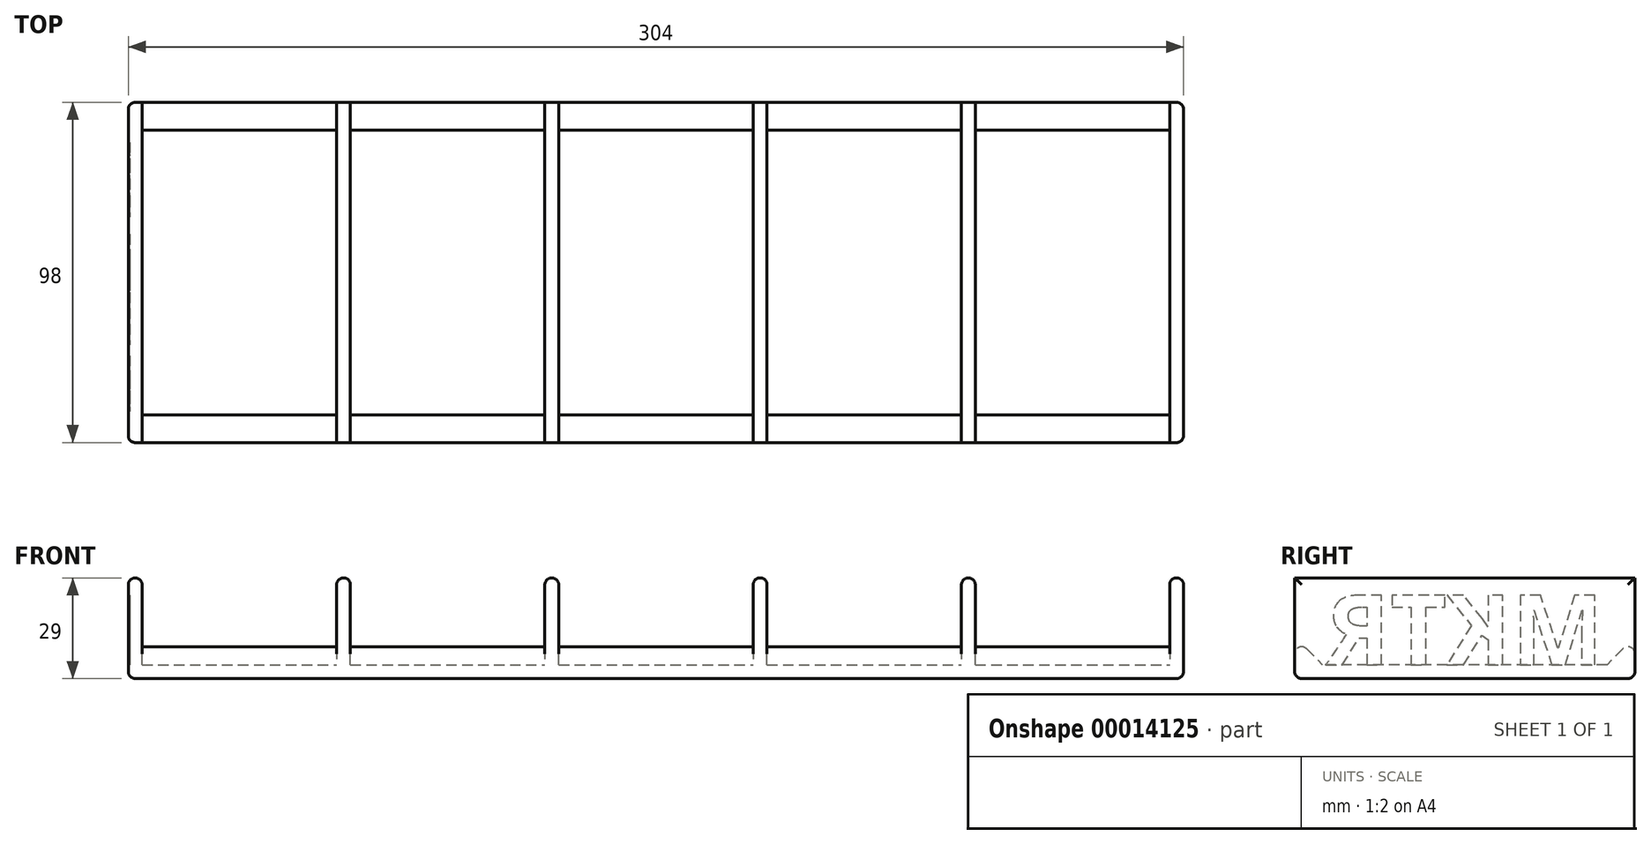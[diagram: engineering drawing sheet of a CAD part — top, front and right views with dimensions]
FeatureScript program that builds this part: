
annotation { "Feature Type Name" : "Feature", "Feature Type Description" : "" }
export const myFeature = defineFeature(function(context is Context, id is Id, definition is map)
    precondition{}
    {
        {
            var Q0;
            Q0=qCreatedBy(makeId("Top.planeOp"),FACE);
            var sketch = newSketch(context, id + "F0", { "sketchPlane" : qUnion([Q0])});
            skLineSegment(sketch, "E0.rect.bottom", {"start": v(-152, 49) * mm, "end": v(152, 49) * mm});
            skLineSegment(sketch, "E0.rect.top", {"start": v(-152, -49) * mm, "end": v(152, -49) * mm});
            skLineSegment(sketch, "E0.rect.left", {"start": v(-152, 49) * mm, "end": v(-152, -49) * mm});
            skLineSegment(sketch, "E0.rect.right", {"start": v(152, 49) * mm, "end": v(152, -49) * mm});
            skPoint(sketch, "E0.rect.middle", {"position": v(0, 0) * mm});
            skSolve(sketch);
        }
        {
            var Q0;
            Q0 = qSketchRegion(id + "F0", true);
            extrude(context, id + "F1", {"entities" : qUnion([Q0]), "depth" : 4 * mm});
        }
        {
            var Q0;
            Q0=makeQuery(id+"F1.opExtrude","CAP_FACE",FACE,{"disambiguationData":[OSD([sQuery(id+"F0.wireOp",EDGE,"E0.rect.bottom"),sQuery(id+"F0.wireOp",EDGE,"E0.rect.top"),sQuery(id+"F0.wireOp",EDGE,"E0.rect.left"),sQuery(id+"F0.wireOp",EDGE,"E0.rect.right")])],"isStart":false});
            var sketch = newSketch(context, id + "F2", { "sketchPlane" : qUnion([Q0])});
            skLineSegment(sketch, "E1.bottom", {"start": v(-152, 49) * mm, "end": v(-148, 49) * mm});
            skLineSegment(sketch, "E1.top", {"start": v(-152, -49) * mm, "end": v(-148, -49) * mm});
            skLineSegment(sketch, "E1.left", {"start": v(-152, 49) * mm, "end": v(-152, -49) * mm});
            skLineSegment(sketch, "E1.right", {"start": v(-148, 49) * mm, "end": v(-148, -49) * mm});
            skLineSegment(sketch, "E2.1.0.0", {"start": v(-88, 49) * mm, "end": v(-88, -49) * mm});
            skLineSegment(sketch, "E2.1.0.1", {"start": v(-92, 49) * mm, "end": v(-92, -49) * mm});
            skLineSegment(sketch, "E2.1.0.2", {"start": v(-92, 49) * mm, "end": v(-88, 49) * mm});
            skLineSegment(sketch, "E2.1.0.3", {"start": v(-92, -49) * mm, "end": v(-88, -49) * mm});
            skLineSegment(sketch, "E2.2.0.0", {"start": v(-28, 49) * mm, "end": v(-28, -49) * mm});
            skLineSegment(sketch, "E2.2.0.1", {"start": v(-32, 49) * mm, "end": v(-32, -49) * mm});
            skLineSegment(sketch, "E2.2.0.2", {"start": v(-32, 49) * mm, "end": v(-28, 49) * mm});
            skLineSegment(sketch, "E2.2.0.3", {"start": v(-32, -49) * mm, "end": v(-28, -49) * mm});
            skLineSegment(sketch, "E2.3.0.0", {"start": v(32, 49) * mm, "end": v(32, -49) * mm});
            skLineSegment(sketch, "E2.3.0.1", {"start": v(28, 49) * mm, "end": v(28, -49) * mm});
            skLineSegment(sketch, "E2.3.0.2", {"start": v(28, 49) * mm, "end": v(32, 49) * mm});
            skLineSegment(sketch, "E2.3.0.3", {"start": v(28, -49) * mm, "end": v(32, -49) * mm});
            skLineSegment(sketch, "E2.4.0.0", {"start": v(92, 49) * mm, "end": v(92, -49) * mm});
            skLineSegment(sketch, "E2.4.0.1", {"start": v(88, 49) * mm, "end": v(88, -49) * mm});
            skLineSegment(sketch, "E2.4.0.2", {"start": v(88, 49) * mm, "end": v(92, 49) * mm});
            skLineSegment(sketch, "E2.4.0.3", {"start": v(88, -49) * mm, "end": v(92, -49) * mm});
            skLineSegment(sketch, "E2.direction1", {"start": v(-148, -49) * mm, "end": v(-88, -49) * mm, "construction": true});
            skLineSegment(sketch, "E3.0.5.0", {"start": v(152, 49) * mm, "end": v(152, -49) * mm});
            skLineSegment(sketch, "E3.3.5.0", {"start": v(148, 49) * mm, "end": v(148, -49) * mm});
            skLineSegment(sketch, "E3.6.5.0", {"start": v(148, 49) * mm, "end": v(152, 49) * mm});
            skLineSegment(sketch, "E3.9.5.0", {"start": v(148, -49) * mm, "end": v(152, -49) * mm});
            skSolve(sketch);
        }
        {
            var Q0;
            Q0 = qSketchRegion(id + "F2", true);
            extrude(context, id + "F3", {"entities" : qUnion([Q0]), "operationType" : NewBodyOperationType.ADD, "depth" : 25 * mm});
        }
        {
            var Q0;
            Q0=makeQuery(id+"F1.opExtrude","CAP_FACE",FACE,{"disambiguationData":[OSD([sQuery(id+"F0.wireOp",EDGE,"E0.rect.bottom"),sQuery(id+"F0.wireOp",EDGE,"E0.rect.top"),sQuery(id+"F0.wireOp",EDGE,"E0.rect.left"),sQuery(id+"F0.wireOp",EDGE,"E0.rect.right")])],"isStart":false});
            var sketch = newSketch(context, id + "F4", { "sketchPlane" : qUnion([Q0])});
            skLineSegment(sketch, "E4.bottom", {"start": v(-148, 49) * mm, "end": v(-92, 49) * mm});
            skLineSegment(sketch, "E4.top", {"start": v(-148, 41) * mm, "end": v(-92, 41) * mm});
            skLineSegment(sketch, "E4.left", {"start": v(-148, 49) * mm, "end": v(-148, 41) * mm});
            skLineSegment(sketch, "E4.right", {"start": v(-92, 49) * mm, "end": v(-92, 41) * mm});
            skLineSegment(sketch, "E5.bottom", {"start": v(-148, -41) * mm, "end": v(-92, -41) * mm});
            skLineSegment(sketch, "E5.top", {"start": v(-148, -49) * mm, "end": v(-92, -49) * mm});
            skLineSegment(sketch, "E5.left", {"start": v(-148, -41) * mm, "end": v(-148, -49) * mm});
            skLineSegment(sketch, "E5.right", {"start": v(-92, -41) * mm, "end": v(-92, -49) * mm});
            skLineSegment(sketch, "E6.1.0.0", {"start": v(-88, 49) * mm, "end": v(-32, 49) * mm});
            skLineSegment(sketch, "E6.1.0.1", {"start": v(-88, 41) * mm, "end": v(-32, 41) * mm});
            skLineSegment(sketch, "E6.1.0.2", {"start": v(-88, 49) * mm, "end": v(-88, 41) * mm});
            skLineSegment(sketch, "E6.1.0.3", {"start": v(-32, 49) * mm, "end": v(-32, 41) * mm});
            skLineSegment(sketch, "E6.1.0.4", {"start": v(-88, -41) * mm, "end": v(-32, -41) * mm});
            skLineSegment(sketch, "E6.1.0.5", {"start": v(-88, -49) * mm, "end": v(-32, -49) * mm});
            skLineSegment(sketch, "E6.1.0.6", {"start": v(-88, -41) * mm, "end": v(-88, -49) * mm});
            skLineSegment(sketch, "E6.1.0.7", {"start": v(-32, -41) * mm, "end": v(-32, -49) * mm});
            skLineSegment(sketch, "E6.2.0.0", {"start": v(-28, 49) * mm, "end": v(28, 49) * mm});
            skLineSegment(sketch, "E6.2.0.1", {"start": v(-28, 41) * mm, "end": v(28, 41) * mm});
            skLineSegment(sketch, "E6.2.0.2", {"start": v(-28, 49) * mm, "end": v(-28, 41) * mm});
            skLineSegment(sketch, "E6.2.0.3", {"start": v(28, 49) * mm, "end": v(28, 41) * mm});
            skLineSegment(sketch, "E6.2.0.4", {"start": v(-28, -41) * mm, "end": v(28, -41) * mm});
            skLineSegment(sketch, "E6.2.0.5", {"start": v(-28, -49) * mm, "end": v(28, -49) * mm});
            skLineSegment(sketch, "E6.2.0.6", {"start": v(-28, -41) * mm, "end": v(-28, -49) * mm});
            skLineSegment(sketch, "E6.2.0.7", {"start": v(28, -41) * mm, "end": v(28, -49) * mm});
            skLineSegment(sketch, "E6.3.0.0", {"start": v(32, 49) * mm, "end": v(88, 49) * mm});
            skLineSegment(sketch, "E6.3.0.1", {"start": v(32, 41) * mm, "end": v(88, 41) * mm});
            skLineSegment(sketch, "E6.3.0.2", {"start": v(32, 49) * mm, "end": v(32, 41) * mm});
            skLineSegment(sketch, "E6.3.0.3", {"start": v(88, 49) * mm, "end": v(88, 41) * mm});
            skLineSegment(sketch, "E6.3.0.4", {"start": v(32, -41) * mm, "end": v(88, -41) * mm});
            skLineSegment(sketch, "E6.3.0.5", {"start": v(32, -49) * mm, "end": v(88, -49) * mm});
            skLineSegment(sketch, "E6.3.0.6", {"start": v(32, -41) * mm, "end": v(32, -49) * mm});
            skLineSegment(sketch, "E6.3.0.7", {"start": v(88, -41) * mm, "end": v(88, -49) * mm});
            skLineSegment(sketch, "E6.direction1", {"start": v(-148, 49) * mm, "end": v(-88, 49) * mm, "construction": true});
            skLineSegment(sketch, "E7.0.4.0", {"start": v(92, 49) * mm, "end": v(148, 49) * mm});
            skLineSegment(sketch, "E7.3.4.0", {"start": v(92, 41) * mm, "end": v(148, 41) * mm});
            skLineSegment(sketch, "E7.6.4.0", {"start": v(92, 49) * mm, "end": v(92, 41) * mm});
            skLineSegment(sketch, "E7.9.4.0", {"start": v(148, 49) * mm, "end": v(148, 41) * mm});
            skLineSegment(sketch, "E7.12.4.0", {"start": v(92, -41) * mm, "end": v(148, -41) * mm});
            skLineSegment(sketch, "E7.15.4.0", {"start": v(92, -49) * mm, "end": v(148, -49) * mm});
            skLineSegment(sketch, "E7.18.4.0", {"start": v(92, -41) * mm, "end": v(92, -49) * mm});
            skLineSegment(sketch, "E7.21.4.0", {"start": v(148, -41) * mm, "end": v(148, -49) * mm});
            skSolve(sketch);
        }
        {
            var Q0;
            Q0 = qSketchRegion(id + "F4", true);
            extrude(context, id + "F5", {"entities" : qUnion([Q0]), "operationType" : NewBodyOperationType.ADD, "depth" : 12 * mm});
        }
        {
            var Q0;
            Q0=makeQuery(id+"F3.opExtrude","CAP_EDGE",EDGE,{"disambiguationData":[OSD([sQuery(id+"F2.wireOp",EDGE,"E1.right")])],"isStart":false});
            var Q1;
            Q1=makeQuery(id+"F3.opExtrude","CAP_EDGE",EDGE,{"disambiguationData":[OSD([sQuery(id+"F2.wireOp",EDGE,"E1.left")])],"isStart":false});
            var Q2;
            Q2=makeQuery(id+"F3.opExtrude","CAP_EDGE",EDGE,{"disambiguationData":[OSD([sQuery(id+"F2.wireOp",EDGE,"E2.1.0.1")])],"isStart":false});
            var Q3;
            Q3=makeQuery(id+"F3.opExtrude","CAP_EDGE",EDGE,{"disambiguationData":[OSD([sQuery(id+"F2.wireOp",EDGE,"E2.1.0.0")])],"isStart":false});
            var Q4;
            Q4=makeQuery(id+"F3.opExtrude","CAP_EDGE",EDGE,{"disambiguationData":[OSD([sQuery(id+"F2.wireOp",EDGE,"E2.2.0.1")])],"isStart":false});
            var Q5;
            Q5=makeQuery(id+"F3.opExtrude","CAP_EDGE",EDGE,{"disambiguationData":[OSD([sQuery(id+"F2.wireOp",EDGE,"E2.2.0.0")])],"isStart":false});
            var Q6;
            Q6=makeQuery(id+"F3.opExtrude","CAP_EDGE",EDGE,{"disambiguationData":[OSD([sQuery(id+"F2.wireOp",EDGE,"E2.3.0.1")])],"isStart":false});
            var Q7;
            Q7=makeQuery(id+"F3.opExtrude","CAP_EDGE",EDGE,{"disambiguationData":[OSD([sQuery(id+"F2.wireOp",EDGE,"E2.3.0.0")])],"isStart":false});
            var Q8;
            Q8=makeQuery(id+"F3.opExtrude","CAP_EDGE",EDGE,{"disambiguationData":[OSD([sQuery(id+"F2.wireOp",EDGE,"E2.4.0.1")])],"isStart":false});
            var Q9;
            Q9=makeQuery(id+"F3.opExtrude","CAP_EDGE",EDGE,{"disambiguationData":[OSD([sQuery(id+"F2.wireOp",EDGE,"E2.4.0.0")])],"isStart":false});
            var Q10;
            Q10=makeQuery(id+"F1.opExtrude","CAP_EDGE",EDGE,{"disambiguationData":[OSD([sQuery(id+"F0.wireOp",EDGE,"E0.rect.top")])],"isStart":true});
            var Q11;
            Q11=makeQuery(id+"F1.opExtrude","CAP_EDGE",EDGE,{"disambiguationData":[OSD([sQuery(id+"F0.wireOp",EDGE,"E0.rect.right")])],"isStart":true});
            var Q12;
            Q12=makeQuery(id+"F1.opExtrude","CAP_EDGE",EDGE,{"disambiguationData":[OSD([sQuery(id+"F0.wireOp",EDGE,"E0.rect.bottom")])],"isStart":true});
            var Q13;
            Q13=makeQuery(id+"F1.opExtrude","CAP_EDGE",EDGE,{"disambiguationData":[OSD([sQuery(id+"F0.wireOp",EDGE,"E0.rect.left")])],"isStart":true});
            var Q14;
            Q14=makeQuery(id+"F3.opExtrude","CAP_EDGE",EDGE,{"disambiguationData":[OSD([sQuery(id+"F2.wireOp",EDGE,"E3.0.5.0")])],"isStart":false});
            var Q15;
            Q15=makeQuery(id+"F3.opExtrude","CAP_EDGE",EDGE,{"disambiguationData":[OSD([sQuery(id+"F2.wireOp",EDGE,"E3.3.5.0")])],"isStart":false});
            var Q16;
            Q16=makeQuery(id+"F3.boolean.opBoolean","MERGE",EDGE,{"derivedFrom":[makeQuery(id+"F1.opExtrude","SWEPT_EDGE",EDGE,{"disambiguationData":[OSD([sQuery(id+"F0.wireOp",EDGE,"E0.rect.top"),sQuery(id+"F0.wireOp",EDGE,"E0.rect.right")])]}),makeQuery(id+"F3.opExtrude","SWEPT_EDGE",EDGE,{"disambiguationData":[OSD([sQuery(id+"F2.wireOp",EDGE,"E3.0.5.0"),sQuery(id+"F2.wireOp",EDGE,"E3.9.5.0")])]})]});
            var Q17;
            Q17=makeQuery(id+"F3.boolean.opBoolean","MERGE",EDGE,{"derivedFrom":[makeQuery(id+"F1.opExtrude","SWEPT_EDGE",EDGE,{"disambiguationData":[OSD([sQuery(id+"F0.wireOp",EDGE,"E0.rect.top"),sQuery(id+"F0.wireOp",EDGE,"E0.rect.left")])]}),makeQuery(id+"F3.opExtrude","SWEPT_EDGE",EDGE,{"disambiguationData":[OSD([sQuery(id+"F2.wireOp",EDGE,"E1.top"),sQuery(id+"F2.wireOp",EDGE,"E1.left")])]})]});
            var Q18;
            Q18=makeQuery(id+"F3.boolean.opBoolean","MERGE",EDGE,{"derivedFrom":[makeQuery(id+"F1.opExtrude","SWEPT_EDGE",EDGE,{"disambiguationData":[OSD([sQuery(id+"F0.wireOp",EDGE,"E0.rect.bottom"),sQuery(id+"F0.wireOp",EDGE,"E0.rect.left")])]}),makeQuery(id+"F3.opExtrude","SWEPT_EDGE",EDGE,{"disambiguationData":[OSD([sQuery(id+"F2.wireOp",EDGE,"E1.bottom"),sQuery(id+"F2.wireOp",EDGE,"E1.left")])]})]});
            var Q19;
            Q19=makeQuery(id+"F3.boolean.opBoolean","MERGE",EDGE,{"derivedFrom":[makeQuery(id+"F1.opExtrude","SWEPT_EDGE",EDGE,{"disambiguationData":[OSD([sQuery(id+"F0.wireOp",EDGE,"E0.rect.bottom"),sQuery(id+"F0.wireOp",EDGE,"E0.rect.right")])]}),makeQuery(id+"F3.opExtrude","SWEPT_EDGE",EDGE,{"disambiguationData":[OSD([sQuery(id+"F2.wireOp",EDGE,"E3.0.5.0"),sQuery(id+"F2.wireOp",EDGE,"E3.6.5.0")])]})]});
            fillet(context, id + "F6", {"entities" : qUnion([Q0, Q1, Q2, Q3, Q4, Q5, Q6, Q7, Q8, Q9, Q10, Q11, Q12, Q13, Q14, Q15, Q16, Q17, Q18, Q19]), "radius" : 2 * mm, "tangentPropagation" : true, "allowEdgeOverflow" : false});
        }
        {
            var Q0;
            Q0=makeQuery(id+"F5.opExtrude","CAP_EDGE",EDGE,{"disambiguationData":[OSD([sQuery(id+"F4.wireOp",EDGE,"E5.bottom")])],"isStart":false});
            var Q1;
            Q1=makeQuery(id+"F5.opExtrude","CAP_EDGE",EDGE,{"disambiguationData":[OSD([sQuery(id+"F4.wireOp",EDGE,"E6.1.0.4")])],"isStart":false});
            var Q2;
            Q2=makeQuery(id+"F5.opExtrude","CAP_EDGE",EDGE,{"disambiguationData":[OSD([sQuery(id+"F4.wireOp",EDGE,"E6.1.0.1")])],"isStart":false});
            var Q3;
            Q3=makeQuery(id+"F5.opExtrude","CAP_EDGE",EDGE,{"disambiguationData":[OSD([sQuery(id+"F4.wireOp",EDGE,"E4.top")])],"isStart":false});
            var Q4;
            Q4=makeQuery(id+"F5.opExtrude","CAP_EDGE",EDGE,{"disambiguationData":[OSD([sQuery(id+"F4.wireOp",EDGE,"E6.2.0.1")])],"isStart":false});
            var Q5;
            Q5=makeQuery(id+"F5.opExtrude","CAP_EDGE",EDGE,{"disambiguationData":[OSD([sQuery(id+"F4.wireOp",EDGE,"E6.2.0.4")])],"isStart":false});
            var Q6;
            Q6=makeQuery(id+"F5.opExtrude","CAP_EDGE",EDGE,{"disambiguationData":[OSD([sQuery(id+"F4.wireOp",EDGE,"E6.3.0.4")])],"isStart":false});
            var Q7;
            Q7=makeQuery(id+"F5.opExtrude","CAP_EDGE",EDGE,{"disambiguationData":[OSD([sQuery(id+"F4.wireOp",EDGE,"E6.3.0.1")])],"isStart":false});
            var Q8;
            Q8=makeQuery(id+"F5.opExtrude","CAP_EDGE",EDGE,{"disambiguationData":[OSD([sQuery(id+"F4.wireOp",EDGE,"E7.3.4.0")])],"isStart":false});
            var Q9;
            Q9=makeQuery(id+"F5.opExtrude","CAP_EDGE",EDGE,{"disambiguationData":[OSD([sQuery(id+"F4.wireOp",EDGE,"E7.12.4.0")])],"isStart":false});
            chamfer(context, id + "F7", {"entities" : qUnion([Q0, Q1, Q2, Q3, Q4, Q5, Q6, Q7, Q8, Q9]), "width" : 12 * mm, "tangentPropagation" : true});
        }
        {
            var Q0;
            Q0=makeQuery(id+"F7.opChamfer","BLEND_EDGE",EDGE,{"blendedFrom":[makeQuery(id+"F5.opExtrude","CAP_EDGE",EDGE,{"disambiguationData":[OSD([sQuery(id+"F4.wireOp",EDGE,"E5.bottom")])],"isStart":false}),makeQuery(id+"F5.boolean.opBoolean","MERGE",FACE,{"derivedFrom":[makeQuery(id+"F3.boolean.opBoolean","MERGE",FACE,{"derivedFrom":[makeQuery(id+"F1.opExtrude","SWEPT_FACE",FACE,{"disambiguationData":[OSD([sQuery(id+"F0.wireOp",EDGE,"E0.rect.top")])]}),makeQuery(id+"F3.opExtrude","SWEPT_FACE",FACE,{"disambiguationData":[OSD([sQuery(id+"F2.wireOp",EDGE,"E1.top")])]}),makeQuery(id+"F3.opExtrude","SWEPT_FACE",FACE,{"disambiguationData":[OSD([sQuery(id+"F2.wireOp",EDGE,"E2.1.0.3")])]}),makeQuery(id+"F3.opExtrude","SWEPT_FACE",FACE,{"disambiguationData":[OSD([sQuery(id+"F2.wireOp",EDGE,"E2.2.0.3")])]}),makeQuery(id+"F3.opExtrude","SWEPT_FACE",FACE,{"disambiguationData":[OSD([sQuery(id+"F2.wireOp",EDGE,"E2.3.0.3")])]}),makeQuery(id+"F3.opExtrude","SWEPT_FACE",FACE,{"disambiguationData":[OSD([sQuery(id+"F2.wireOp",EDGE,"E2.4.0.3")])]})]}),makeQuery(id+"F5.opExtrude","SWEPT_FACE",FACE,{"disambiguationData":[OSD([sQuery(id+"F4.wireOp",EDGE,"E5.top")])]}),makeQuery(id+"F5.opExtrude","SWEPT_FACE",FACE,{"disambiguationData":[OSD([sQuery(id+"F4.wireOp",EDGE,"E6.1.0.5")])]}),makeQuery(id+"F5.opExtrude","SWEPT_FACE",FACE,{"disambiguationData":[OSD([sQuery(id+"F4.wireOp",EDGE,"E6.2.0.5")])]}),makeQuery(id+"F5.opExtrude","SWEPT_FACE",FACE,{"disambiguationData":[OSD([sQuery(id+"F4.wireOp",EDGE,"E6.3.0.5")])]})]})],"blendedInto":[makeQuery(id+"F5.boolean.opBoolean","MERGE",FACE,{"derivedFrom":[makeQuery(id+"F3.boolean.opBoolean","MERGE",FACE,{"derivedFrom":[makeQuery(id+"F1.opExtrude","SWEPT_FACE",FACE,{"disambiguationData":[OSD([sQuery(id+"F0.wireOp",EDGE,"E0.rect.top")])]}),makeQuery(id+"F3.opExtrude","SWEPT_FACE",FACE,{"disambiguationData":[OSD([sQuery(id+"F2.wireOp",EDGE,"E1.top")])]}),makeQuery(id+"F3.opExtrude","SWEPT_FACE",FACE,{"disambiguationData":[OSD([sQuery(id+"F2.wireOp",EDGE,"E2.1.0.3")])]}),makeQuery(id+"F3.opExtrude","SWEPT_FACE",FACE,{"disambiguationData":[OSD([sQuery(id+"F2.wireOp",EDGE,"E2.2.0.3")])]}),makeQuery(id+"F3.opExtrude","SWEPT_FACE",FACE,{"disambiguationData":[OSD([sQuery(id+"F2.wireOp",EDGE,"E2.3.0.3")])]}),makeQuery(id+"F3.opExtrude","SWEPT_FACE",FACE,{"disambiguationData":[OSD([sQuery(id+"F2.wireOp",EDGE,"E2.4.0.3")])]})]}),makeQuery(id+"F5.opExtrude","SWEPT_FACE",FACE,{"disambiguationData":[OSD([sQuery(id+"F4.wireOp",EDGE,"E5.top")])]}),makeQuery(id+"F5.opExtrude","SWEPT_FACE",FACE,{"disambiguationData":[OSD([sQuery(id+"F4.wireOp",EDGE,"E6.1.0.5")])]}),makeQuery(id+"F5.opExtrude","SWEPT_FACE",FACE,{"disambiguationData":[OSD([sQuery(id+"F4.wireOp",EDGE,"E6.2.0.5")])]}),makeQuery(id+"F5.opExtrude","SWEPT_FACE",FACE,{"disambiguationData":[OSD([sQuery(id+"F4.wireOp",EDGE,"E6.3.0.5")])]})]})]});
            var Q1;
            Q1=makeQuery(id+"F7.opChamfer","BLEND_EDGE",EDGE,{"blendedFrom":[makeQuery(id+"F5.opExtrude","CAP_EDGE",EDGE,{"disambiguationData":[OSD([sQuery(id+"F4.wireOp",EDGE,"E4.top")])],"isStart":false}),makeQuery(id+"F5.boolean.opBoolean","MERGE",FACE,{"derivedFrom":[makeQuery(id+"F3.boolean.opBoolean","MERGE",FACE,{"derivedFrom":[makeQuery(id+"F1.opExtrude","SWEPT_FACE",FACE,{"disambiguationData":[OSD([sQuery(id+"F0.wireOp",EDGE,"E0.rect.bottom")])]}),makeQuery(id+"F3.opExtrude","SWEPT_FACE",FACE,{"disambiguationData":[OSD([sQuery(id+"F2.wireOp",EDGE,"E1.bottom")])]}),makeQuery(id+"F3.opExtrude","SWEPT_FACE",FACE,{"disambiguationData":[OSD([sQuery(id+"F2.wireOp",EDGE,"E2.1.0.2")])]}),makeQuery(id+"F3.opExtrude","SWEPT_FACE",FACE,{"disambiguationData":[OSD([sQuery(id+"F2.wireOp",EDGE,"E2.2.0.2")])]}),makeQuery(id+"F3.opExtrude","SWEPT_FACE",FACE,{"disambiguationData":[OSD([sQuery(id+"F2.wireOp",EDGE,"E2.3.0.2")])]}),makeQuery(id+"F3.opExtrude","SWEPT_FACE",FACE,{"disambiguationData":[OSD([sQuery(id+"F2.wireOp",EDGE,"E2.4.0.2")])]})]}),makeQuery(id+"F5.opExtrude","SWEPT_FACE",FACE,{"disambiguationData":[OSD([sQuery(id+"F4.wireOp",EDGE,"E4.bottom")])]}),makeQuery(id+"F5.opExtrude","SWEPT_FACE",FACE,{"disambiguationData":[OSD([sQuery(id+"F4.wireOp",EDGE,"E6.1.0.0")])]}),makeQuery(id+"F5.opExtrude","SWEPT_FACE",FACE,{"disambiguationData":[OSD([sQuery(id+"F4.wireOp",EDGE,"E6.2.0.0")])]}),makeQuery(id+"F5.opExtrude","SWEPT_FACE",FACE,{"disambiguationData":[OSD([sQuery(id+"F4.wireOp",EDGE,"E6.3.0.0")])]})]})],"blendedInto":[makeQuery(id+"F5.boolean.opBoolean","MERGE",FACE,{"derivedFrom":[makeQuery(id+"F3.boolean.opBoolean","MERGE",FACE,{"derivedFrom":[makeQuery(id+"F1.opExtrude","SWEPT_FACE",FACE,{"disambiguationData":[OSD([sQuery(id+"F0.wireOp",EDGE,"E0.rect.bottom")])]}),makeQuery(id+"F3.opExtrude","SWEPT_FACE",FACE,{"disambiguationData":[OSD([sQuery(id+"F2.wireOp",EDGE,"E1.bottom")])]}),makeQuery(id+"F3.opExtrude","SWEPT_FACE",FACE,{"disambiguationData":[OSD([sQuery(id+"F2.wireOp",EDGE,"E2.1.0.2")])]}),makeQuery(id+"F3.opExtrude","SWEPT_FACE",FACE,{"disambiguationData":[OSD([sQuery(id+"F2.wireOp",EDGE,"E2.2.0.2")])]}),makeQuery(id+"F3.opExtrude","SWEPT_FACE",FACE,{"disambiguationData":[OSD([sQuery(id+"F2.wireOp",EDGE,"E2.3.0.2")])]}),makeQuery(id+"F3.opExtrude","SWEPT_FACE",FACE,{"disambiguationData":[OSD([sQuery(id+"F2.wireOp",EDGE,"E2.4.0.2")])]})]}),makeQuery(id+"F5.opExtrude","SWEPT_FACE",FACE,{"disambiguationData":[OSD([sQuery(id+"F4.wireOp",EDGE,"E4.bottom")])]}),makeQuery(id+"F5.opExtrude","SWEPT_FACE",FACE,{"disambiguationData":[OSD([sQuery(id+"F4.wireOp",EDGE,"E6.1.0.0")])]}),makeQuery(id+"F5.opExtrude","SWEPT_FACE",FACE,{"disambiguationData":[OSD([sQuery(id+"F4.wireOp",EDGE,"E6.2.0.0")])]}),makeQuery(id+"F5.opExtrude","SWEPT_FACE",FACE,{"disambiguationData":[OSD([sQuery(id+"F4.wireOp",EDGE,"E6.3.0.0")])]})]})]});
            var Q2;
            Q2=makeQuery(id+"F7.opChamfer","BLEND_EDGE",EDGE,{"blendedFrom":[makeQuery(id+"F5.opExtrude","CAP_EDGE",EDGE,{"disambiguationData":[OSD([sQuery(id+"F4.wireOp",EDGE,"E6.1.0.1")])],"isStart":false}),makeQuery(id+"F5.boolean.opBoolean","MERGE",FACE,{"derivedFrom":[makeQuery(id+"F3.boolean.opBoolean","MERGE",FACE,{"derivedFrom":[makeQuery(id+"F1.opExtrude","SWEPT_FACE",FACE,{"disambiguationData":[OSD([sQuery(id+"F0.wireOp",EDGE,"E0.rect.bottom")])]}),makeQuery(id+"F3.opExtrude","SWEPT_FACE",FACE,{"disambiguationData":[OSD([sQuery(id+"F2.wireOp",EDGE,"E1.bottom")])]}),makeQuery(id+"F3.opExtrude","SWEPT_FACE",FACE,{"disambiguationData":[OSD([sQuery(id+"F2.wireOp",EDGE,"E2.1.0.2")])]}),makeQuery(id+"F3.opExtrude","SWEPT_FACE",FACE,{"disambiguationData":[OSD([sQuery(id+"F2.wireOp",EDGE,"E2.2.0.2")])]}),makeQuery(id+"F3.opExtrude","SWEPT_FACE",FACE,{"disambiguationData":[OSD([sQuery(id+"F2.wireOp",EDGE,"E2.3.0.2")])]}),makeQuery(id+"F3.opExtrude","SWEPT_FACE",FACE,{"disambiguationData":[OSD([sQuery(id+"F2.wireOp",EDGE,"E2.4.0.2")])]})]}),makeQuery(id+"F5.opExtrude","SWEPT_FACE",FACE,{"disambiguationData":[OSD([sQuery(id+"F4.wireOp",EDGE,"E4.bottom")])]}),makeQuery(id+"F5.opExtrude","SWEPT_FACE",FACE,{"disambiguationData":[OSD([sQuery(id+"F4.wireOp",EDGE,"E6.1.0.0")])]}),makeQuery(id+"F5.opExtrude","SWEPT_FACE",FACE,{"disambiguationData":[OSD([sQuery(id+"F4.wireOp",EDGE,"E6.2.0.0")])]}),makeQuery(id+"F5.opExtrude","SWEPT_FACE",FACE,{"disambiguationData":[OSD([sQuery(id+"F4.wireOp",EDGE,"E6.3.0.0")])]})]})],"blendedInto":[makeQuery(id+"F5.boolean.opBoolean","MERGE",FACE,{"derivedFrom":[makeQuery(id+"F3.boolean.opBoolean","MERGE",FACE,{"derivedFrom":[makeQuery(id+"F1.opExtrude","SWEPT_FACE",FACE,{"disambiguationData":[OSD([sQuery(id+"F0.wireOp",EDGE,"E0.rect.bottom")])]}),makeQuery(id+"F3.opExtrude","SWEPT_FACE",FACE,{"disambiguationData":[OSD([sQuery(id+"F2.wireOp",EDGE,"E1.bottom")])]}),makeQuery(id+"F3.opExtrude","SWEPT_FACE",FACE,{"disambiguationData":[OSD([sQuery(id+"F2.wireOp",EDGE,"E2.1.0.2")])]}),makeQuery(id+"F3.opExtrude","SWEPT_FACE",FACE,{"disambiguationData":[OSD([sQuery(id+"F2.wireOp",EDGE,"E2.2.0.2")])]}),makeQuery(id+"F3.opExtrude","SWEPT_FACE",FACE,{"disambiguationData":[OSD([sQuery(id+"F2.wireOp",EDGE,"E2.3.0.2")])]}),makeQuery(id+"F3.opExtrude","SWEPT_FACE",FACE,{"disambiguationData":[OSD([sQuery(id+"F2.wireOp",EDGE,"E2.4.0.2")])]})]}),makeQuery(id+"F5.opExtrude","SWEPT_FACE",FACE,{"disambiguationData":[OSD([sQuery(id+"F4.wireOp",EDGE,"E4.bottom")])]}),makeQuery(id+"F5.opExtrude","SWEPT_FACE",FACE,{"disambiguationData":[OSD([sQuery(id+"F4.wireOp",EDGE,"E6.1.0.0")])]}),makeQuery(id+"F5.opExtrude","SWEPT_FACE",FACE,{"disambiguationData":[OSD([sQuery(id+"F4.wireOp",EDGE,"E6.2.0.0")])]}),makeQuery(id+"F5.opExtrude","SWEPT_FACE",FACE,{"disambiguationData":[OSD([sQuery(id+"F4.wireOp",EDGE,"E6.3.0.0")])]})]})]});
            var Q3;
            Q3=makeQuery(id+"F7.opChamfer","BLEND_EDGE",EDGE,{"blendedFrom":[makeQuery(id+"F5.opExtrude","CAP_EDGE",EDGE,{"disambiguationData":[OSD([sQuery(id+"F4.wireOp",EDGE,"E6.1.0.4")])],"isStart":false}),makeQuery(id+"F5.boolean.opBoolean","MERGE",FACE,{"derivedFrom":[makeQuery(id+"F3.boolean.opBoolean","MERGE",FACE,{"derivedFrom":[makeQuery(id+"F1.opExtrude","SWEPT_FACE",FACE,{"disambiguationData":[OSD([sQuery(id+"F0.wireOp",EDGE,"E0.rect.top")])]}),makeQuery(id+"F3.opExtrude","SWEPT_FACE",FACE,{"disambiguationData":[OSD([sQuery(id+"F2.wireOp",EDGE,"E1.top")])]}),makeQuery(id+"F3.opExtrude","SWEPT_FACE",FACE,{"disambiguationData":[OSD([sQuery(id+"F2.wireOp",EDGE,"E2.1.0.3")])]}),makeQuery(id+"F3.opExtrude","SWEPT_FACE",FACE,{"disambiguationData":[OSD([sQuery(id+"F2.wireOp",EDGE,"E2.2.0.3")])]}),makeQuery(id+"F3.opExtrude","SWEPT_FACE",FACE,{"disambiguationData":[OSD([sQuery(id+"F2.wireOp",EDGE,"E2.3.0.3")])]}),makeQuery(id+"F3.opExtrude","SWEPT_FACE",FACE,{"disambiguationData":[OSD([sQuery(id+"F2.wireOp",EDGE,"E2.4.0.3")])]})]}),makeQuery(id+"F5.opExtrude","SWEPT_FACE",FACE,{"disambiguationData":[OSD([sQuery(id+"F4.wireOp",EDGE,"E5.top")])]}),makeQuery(id+"F5.opExtrude","SWEPT_FACE",FACE,{"disambiguationData":[OSD([sQuery(id+"F4.wireOp",EDGE,"E6.1.0.5")])]}),makeQuery(id+"F5.opExtrude","SWEPT_FACE",FACE,{"disambiguationData":[OSD([sQuery(id+"F4.wireOp",EDGE,"E6.2.0.5")])]}),makeQuery(id+"F5.opExtrude","SWEPT_FACE",FACE,{"disambiguationData":[OSD([sQuery(id+"F4.wireOp",EDGE,"E6.3.0.5")])]})]})],"blendedInto":[makeQuery(id+"F5.boolean.opBoolean","MERGE",FACE,{"derivedFrom":[makeQuery(id+"F3.boolean.opBoolean","MERGE",FACE,{"derivedFrom":[makeQuery(id+"F1.opExtrude","SWEPT_FACE",FACE,{"disambiguationData":[OSD([sQuery(id+"F0.wireOp",EDGE,"E0.rect.top")])]}),makeQuery(id+"F3.opExtrude","SWEPT_FACE",FACE,{"disambiguationData":[OSD([sQuery(id+"F2.wireOp",EDGE,"E1.top")])]}),makeQuery(id+"F3.opExtrude","SWEPT_FACE",FACE,{"disambiguationData":[OSD([sQuery(id+"F2.wireOp",EDGE,"E2.1.0.3")])]}),makeQuery(id+"F3.opExtrude","SWEPT_FACE",FACE,{"disambiguationData":[OSD([sQuery(id+"F2.wireOp",EDGE,"E2.2.0.3")])]}),makeQuery(id+"F3.opExtrude","SWEPT_FACE",FACE,{"disambiguationData":[OSD([sQuery(id+"F2.wireOp",EDGE,"E2.3.0.3")])]}),makeQuery(id+"F3.opExtrude","SWEPT_FACE",FACE,{"disambiguationData":[OSD([sQuery(id+"F2.wireOp",EDGE,"E2.4.0.3")])]})]}),makeQuery(id+"F5.opExtrude","SWEPT_FACE",FACE,{"disambiguationData":[OSD([sQuery(id+"F4.wireOp",EDGE,"E5.top")])]}),makeQuery(id+"F5.opExtrude","SWEPT_FACE",FACE,{"disambiguationData":[OSD([sQuery(id+"F4.wireOp",EDGE,"E6.1.0.5")])]}),makeQuery(id+"F5.opExtrude","SWEPT_FACE",FACE,{"disambiguationData":[OSD([sQuery(id+"F4.wireOp",EDGE,"E6.2.0.5")])]}),makeQuery(id+"F5.opExtrude","SWEPT_FACE",FACE,{"disambiguationData":[OSD([sQuery(id+"F4.wireOp",EDGE,"E6.3.0.5")])]})]})]});
            var Q4;
            Q4=makeQuery(id+"F7.opChamfer","BLEND_EDGE",EDGE,{"blendedFrom":[makeQuery(id+"F5.opExtrude","CAP_EDGE",EDGE,{"disambiguationData":[OSD([sQuery(id+"F4.wireOp",EDGE,"E6.2.0.4")])],"isStart":false}),makeQuery(id+"F5.boolean.opBoolean","MERGE",FACE,{"derivedFrom":[makeQuery(id+"F3.boolean.opBoolean","MERGE",FACE,{"derivedFrom":[makeQuery(id+"F1.opExtrude","SWEPT_FACE",FACE,{"disambiguationData":[OSD([sQuery(id+"F0.wireOp",EDGE,"E0.rect.top")])]}),makeQuery(id+"F3.opExtrude","SWEPT_FACE",FACE,{"disambiguationData":[OSD([sQuery(id+"F2.wireOp",EDGE,"E1.top")])]}),makeQuery(id+"F3.opExtrude","SWEPT_FACE",FACE,{"disambiguationData":[OSD([sQuery(id+"F2.wireOp",EDGE,"E2.1.0.3")])]}),makeQuery(id+"F3.opExtrude","SWEPT_FACE",FACE,{"disambiguationData":[OSD([sQuery(id+"F2.wireOp",EDGE,"E2.2.0.3")])]}),makeQuery(id+"F3.opExtrude","SWEPT_FACE",FACE,{"disambiguationData":[OSD([sQuery(id+"F2.wireOp",EDGE,"E2.3.0.3")])]}),makeQuery(id+"F3.opExtrude","SWEPT_FACE",FACE,{"disambiguationData":[OSD([sQuery(id+"F2.wireOp",EDGE,"E2.4.0.3")])]})]}),makeQuery(id+"F5.opExtrude","SWEPT_FACE",FACE,{"disambiguationData":[OSD([sQuery(id+"F4.wireOp",EDGE,"E5.top")])]}),makeQuery(id+"F5.opExtrude","SWEPT_FACE",FACE,{"disambiguationData":[OSD([sQuery(id+"F4.wireOp",EDGE,"E6.1.0.5")])]}),makeQuery(id+"F5.opExtrude","SWEPT_FACE",FACE,{"disambiguationData":[OSD([sQuery(id+"F4.wireOp",EDGE,"E6.2.0.5")])]}),makeQuery(id+"F5.opExtrude","SWEPT_FACE",FACE,{"disambiguationData":[OSD([sQuery(id+"F4.wireOp",EDGE,"E6.3.0.5")])]})]})],"blendedInto":[makeQuery(id+"F5.boolean.opBoolean","MERGE",FACE,{"derivedFrom":[makeQuery(id+"F3.boolean.opBoolean","MERGE",FACE,{"derivedFrom":[makeQuery(id+"F1.opExtrude","SWEPT_FACE",FACE,{"disambiguationData":[OSD([sQuery(id+"F0.wireOp",EDGE,"E0.rect.top")])]}),makeQuery(id+"F3.opExtrude","SWEPT_FACE",FACE,{"disambiguationData":[OSD([sQuery(id+"F2.wireOp",EDGE,"E1.top")])]}),makeQuery(id+"F3.opExtrude","SWEPT_FACE",FACE,{"disambiguationData":[OSD([sQuery(id+"F2.wireOp",EDGE,"E2.1.0.3")])]}),makeQuery(id+"F3.opExtrude","SWEPT_FACE",FACE,{"disambiguationData":[OSD([sQuery(id+"F2.wireOp",EDGE,"E2.2.0.3")])]}),makeQuery(id+"F3.opExtrude","SWEPT_FACE",FACE,{"disambiguationData":[OSD([sQuery(id+"F2.wireOp",EDGE,"E2.3.0.3")])]}),makeQuery(id+"F3.opExtrude","SWEPT_FACE",FACE,{"disambiguationData":[OSD([sQuery(id+"F2.wireOp",EDGE,"E2.4.0.3")])]})]}),makeQuery(id+"F5.opExtrude","SWEPT_FACE",FACE,{"disambiguationData":[OSD([sQuery(id+"F4.wireOp",EDGE,"E5.top")])]}),makeQuery(id+"F5.opExtrude","SWEPT_FACE",FACE,{"disambiguationData":[OSD([sQuery(id+"F4.wireOp",EDGE,"E6.1.0.5")])]}),makeQuery(id+"F5.opExtrude","SWEPT_FACE",FACE,{"disambiguationData":[OSD([sQuery(id+"F4.wireOp",EDGE,"E6.2.0.5")])]}),makeQuery(id+"F5.opExtrude","SWEPT_FACE",FACE,{"disambiguationData":[OSD([sQuery(id+"F4.wireOp",EDGE,"E6.3.0.5")])]})]})]});
            var Q5;
            Q5=makeQuery(id+"F7.opChamfer","BLEND_EDGE",EDGE,{"blendedFrom":[makeQuery(id+"F5.opExtrude","CAP_EDGE",EDGE,{"disambiguationData":[OSD([sQuery(id+"F4.wireOp",EDGE,"E6.2.0.1")])],"isStart":false}),makeQuery(id+"F5.boolean.opBoolean","MERGE",FACE,{"derivedFrom":[makeQuery(id+"F3.boolean.opBoolean","MERGE",FACE,{"derivedFrom":[makeQuery(id+"F1.opExtrude","SWEPT_FACE",FACE,{"disambiguationData":[OSD([sQuery(id+"F0.wireOp",EDGE,"E0.rect.bottom")])]}),makeQuery(id+"F3.opExtrude","SWEPT_FACE",FACE,{"disambiguationData":[OSD([sQuery(id+"F2.wireOp",EDGE,"E1.bottom")])]}),makeQuery(id+"F3.opExtrude","SWEPT_FACE",FACE,{"disambiguationData":[OSD([sQuery(id+"F2.wireOp",EDGE,"E2.1.0.2")])]}),makeQuery(id+"F3.opExtrude","SWEPT_FACE",FACE,{"disambiguationData":[OSD([sQuery(id+"F2.wireOp",EDGE,"E2.2.0.2")])]}),makeQuery(id+"F3.opExtrude","SWEPT_FACE",FACE,{"disambiguationData":[OSD([sQuery(id+"F2.wireOp",EDGE,"E2.3.0.2")])]}),makeQuery(id+"F3.opExtrude","SWEPT_FACE",FACE,{"disambiguationData":[OSD([sQuery(id+"F2.wireOp",EDGE,"E2.4.0.2")])]})]}),makeQuery(id+"F5.opExtrude","SWEPT_FACE",FACE,{"disambiguationData":[OSD([sQuery(id+"F4.wireOp",EDGE,"E4.bottom")])]}),makeQuery(id+"F5.opExtrude","SWEPT_FACE",FACE,{"disambiguationData":[OSD([sQuery(id+"F4.wireOp",EDGE,"E6.1.0.0")])]}),makeQuery(id+"F5.opExtrude","SWEPT_FACE",FACE,{"disambiguationData":[OSD([sQuery(id+"F4.wireOp",EDGE,"E6.2.0.0")])]}),makeQuery(id+"F5.opExtrude","SWEPT_FACE",FACE,{"disambiguationData":[OSD([sQuery(id+"F4.wireOp",EDGE,"E6.3.0.0")])]})]})],"blendedInto":[makeQuery(id+"F5.boolean.opBoolean","MERGE",FACE,{"derivedFrom":[makeQuery(id+"F3.boolean.opBoolean","MERGE",FACE,{"derivedFrom":[makeQuery(id+"F1.opExtrude","SWEPT_FACE",FACE,{"disambiguationData":[OSD([sQuery(id+"F0.wireOp",EDGE,"E0.rect.bottom")])]}),makeQuery(id+"F3.opExtrude","SWEPT_FACE",FACE,{"disambiguationData":[OSD([sQuery(id+"F2.wireOp",EDGE,"E1.bottom")])]}),makeQuery(id+"F3.opExtrude","SWEPT_FACE",FACE,{"disambiguationData":[OSD([sQuery(id+"F2.wireOp",EDGE,"E2.1.0.2")])]}),makeQuery(id+"F3.opExtrude","SWEPT_FACE",FACE,{"disambiguationData":[OSD([sQuery(id+"F2.wireOp",EDGE,"E2.2.0.2")])]}),makeQuery(id+"F3.opExtrude","SWEPT_FACE",FACE,{"disambiguationData":[OSD([sQuery(id+"F2.wireOp",EDGE,"E2.3.0.2")])]}),makeQuery(id+"F3.opExtrude","SWEPT_FACE",FACE,{"disambiguationData":[OSD([sQuery(id+"F2.wireOp",EDGE,"E2.4.0.2")])]})]}),makeQuery(id+"F5.opExtrude","SWEPT_FACE",FACE,{"disambiguationData":[OSD([sQuery(id+"F4.wireOp",EDGE,"E4.bottom")])]}),makeQuery(id+"F5.opExtrude","SWEPT_FACE",FACE,{"disambiguationData":[OSD([sQuery(id+"F4.wireOp",EDGE,"E6.1.0.0")])]}),makeQuery(id+"F5.opExtrude","SWEPT_FACE",FACE,{"disambiguationData":[OSD([sQuery(id+"F4.wireOp",EDGE,"E6.2.0.0")])]}),makeQuery(id+"F5.opExtrude","SWEPT_FACE",FACE,{"disambiguationData":[OSD([sQuery(id+"F4.wireOp",EDGE,"E6.3.0.0")])]})]})]});
            var Q6;
            Q6=makeQuery(id+"F7.opChamfer","BLEND_EDGE",EDGE,{"blendedFrom":[makeQuery(id+"F5.opExtrude","CAP_EDGE",EDGE,{"disambiguationData":[OSD([sQuery(id+"F4.wireOp",EDGE,"E6.3.0.1")])],"isStart":false}),makeQuery(id+"F5.boolean.opBoolean","MERGE",FACE,{"derivedFrom":[makeQuery(id+"F3.boolean.opBoolean","MERGE",FACE,{"derivedFrom":[makeQuery(id+"F1.opExtrude","SWEPT_FACE",FACE,{"disambiguationData":[OSD([sQuery(id+"F0.wireOp",EDGE,"E0.rect.bottom")])]}),makeQuery(id+"F3.opExtrude","SWEPT_FACE",FACE,{"disambiguationData":[OSD([sQuery(id+"F2.wireOp",EDGE,"E1.bottom")])]}),makeQuery(id+"F3.opExtrude","SWEPT_FACE",FACE,{"disambiguationData":[OSD([sQuery(id+"F2.wireOp",EDGE,"E2.1.0.2")])]}),makeQuery(id+"F3.opExtrude","SWEPT_FACE",FACE,{"disambiguationData":[OSD([sQuery(id+"F2.wireOp",EDGE,"E2.2.0.2")])]}),makeQuery(id+"F3.opExtrude","SWEPT_FACE",FACE,{"disambiguationData":[OSD([sQuery(id+"F2.wireOp",EDGE,"E2.3.0.2")])]}),makeQuery(id+"F3.opExtrude","SWEPT_FACE",FACE,{"disambiguationData":[OSD([sQuery(id+"F2.wireOp",EDGE,"E2.4.0.2")])]})]}),makeQuery(id+"F5.opExtrude","SWEPT_FACE",FACE,{"disambiguationData":[OSD([sQuery(id+"F4.wireOp",EDGE,"E4.bottom")])]}),makeQuery(id+"F5.opExtrude","SWEPT_FACE",FACE,{"disambiguationData":[OSD([sQuery(id+"F4.wireOp",EDGE,"E6.1.0.0")])]}),makeQuery(id+"F5.opExtrude","SWEPT_FACE",FACE,{"disambiguationData":[OSD([sQuery(id+"F4.wireOp",EDGE,"E6.2.0.0")])]}),makeQuery(id+"F5.opExtrude","SWEPT_FACE",FACE,{"disambiguationData":[OSD([sQuery(id+"F4.wireOp",EDGE,"E6.3.0.0")])]})]})],"blendedInto":[makeQuery(id+"F5.boolean.opBoolean","MERGE",FACE,{"derivedFrom":[makeQuery(id+"F3.boolean.opBoolean","MERGE",FACE,{"derivedFrom":[makeQuery(id+"F1.opExtrude","SWEPT_FACE",FACE,{"disambiguationData":[OSD([sQuery(id+"F0.wireOp",EDGE,"E0.rect.bottom")])]}),makeQuery(id+"F3.opExtrude","SWEPT_FACE",FACE,{"disambiguationData":[OSD([sQuery(id+"F2.wireOp",EDGE,"E1.bottom")])]}),makeQuery(id+"F3.opExtrude","SWEPT_FACE",FACE,{"disambiguationData":[OSD([sQuery(id+"F2.wireOp",EDGE,"E2.1.0.2")])]}),makeQuery(id+"F3.opExtrude","SWEPT_FACE",FACE,{"disambiguationData":[OSD([sQuery(id+"F2.wireOp",EDGE,"E2.2.0.2")])]}),makeQuery(id+"F3.opExtrude","SWEPT_FACE",FACE,{"disambiguationData":[OSD([sQuery(id+"F2.wireOp",EDGE,"E2.3.0.2")])]}),makeQuery(id+"F3.opExtrude","SWEPT_FACE",FACE,{"disambiguationData":[OSD([sQuery(id+"F2.wireOp",EDGE,"E2.4.0.2")])]})]}),makeQuery(id+"F5.opExtrude","SWEPT_FACE",FACE,{"disambiguationData":[OSD([sQuery(id+"F4.wireOp",EDGE,"E4.bottom")])]}),makeQuery(id+"F5.opExtrude","SWEPT_FACE",FACE,{"disambiguationData":[OSD([sQuery(id+"F4.wireOp",EDGE,"E6.1.0.0")])]}),makeQuery(id+"F5.opExtrude","SWEPT_FACE",FACE,{"disambiguationData":[OSD([sQuery(id+"F4.wireOp",EDGE,"E6.2.0.0")])]}),makeQuery(id+"F5.opExtrude","SWEPT_FACE",FACE,{"disambiguationData":[OSD([sQuery(id+"F4.wireOp",EDGE,"E6.3.0.0")])]})]})]});
            var Q7;
            Q7=makeQuery(id+"F7.opChamfer","BLEND_EDGE",EDGE,{"blendedFrom":[makeQuery(id+"F5.opExtrude","CAP_EDGE",EDGE,{"disambiguationData":[OSD([sQuery(id+"F4.wireOp",EDGE,"E6.3.0.4")])],"isStart":false}),makeQuery(id+"F5.boolean.opBoolean","MERGE",FACE,{"derivedFrom":[makeQuery(id+"F3.boolean.opBoolean","MERGE",FACE,{"derivedFrom":[makeQuery(id+"F1.opExtrude","SWEPT_FACE",FACE,{"disambiguationData":[OSD([sQuery(id+"F0.wireOp",EDGE,"E0.rect.top")])]}),makeQuery(id+"F3.opExtrude","SWEPT_FACE",FACE,{"disambiguationData":[OSD([sQuery(id+"F2.wireOp",EDGE,"E1.top")])]}),makeQuery(id+"F3.opExtrude","SWEPT_FACE",FACE,{"disambiguationData":[OSD([sQuery(id+"F2.wireOp",EDGE,"E2.1.0.3")])]}),makeQuery(id+"F3.opExtrude","SWEPT_FACE",FACE,{"disambiguationData":[OSD([sQuery(id+"F2.wireOp",EDGE,"E2.2.0.3")])]}),makeQuery(id+"F3.opExtrude","SWEPT_FACE",FACE,{"disambiguationData":[OSD([sQuery(id+"F2.wireOp",EDGE,"E2.3.0.3")])]}),makeQuery(id+"F3.opExtrude","SWEPT_FACE",FACE,{"disambiguationData":[OSD([sQuery(id+"F2.wireOp",EDGE,"E2.4.0.3")])]})]}),makeQuery(id+"F5.opExtrude","SWEPT_FACE",FACE,{"disambiguationData":[OSD([sQuery(id+"F4.wireOp",EDGE,"E5.top")])]}),makeQuery(id+"F5.opExtrude","SWEPT_FACE",FACE,{"disambiguationData":[OSD([sQuery(id+"F4.wireOp",EDGE,"E6.1.0.5")])]}),makeQuery(id+"F5.opExtrude","SWEPT_FACE",FACE,{"disambiguationData":[OSD([sQuery(id+"F4.wireOp",EDGE,"E6.2.0.5")])]}),makeQuery(id+"F5.opExtrude","SWEPT_FACE",FACE,{"disambiguationData":[OSD([sQuery(id+"F4.wireOp",EDGE,"E6.3.0.5")])]})]})],"blendedInto":[makeQuery(id+"F5.boolean.opBoolean","MERGE",FACE,{"derivedFrom":[makeQuery(id+"F3.boolean.opBoolean","MERGE",FACE,{"derivedFrom":[makeQuery(id+"F1.opExtrude","SWEPT_FACE",FACE,{"disambiguationData":[OSD([sQuery(id+"F0.wireOp",EDGE,"E0.rect.top")])]}),makeQuery(id+"F3.opExtrude","SWEPT_FACE",FACE,{"disambiguationData":[OSD([sQuery(id+"F2.wireOp",EDGE,"E1.top")])]}),makeQuery(id+"F3.opExtrude","SWEPT_FACE",FACE,{"disambiguationData":[OSD([sQuery(id+"F2.wireOp",EDGE,"E2.1.0.3")])]}),makeQuery(id+"F3.opExtrude","SWEPT_FACE",FACE,{"disambiguationData":[OSD([sQuery(id+"F2.wireOp",EDGE,"E2.2.0.3")])]}),makeQuery(id+"F3.opExtrude","SWEPT_FACE",FACE,{"disambiguationData":[OSD([sQuery(id+"F2.wireOp",EDGE,"E2.3.0.3")])]}),makeQuery(id+"F3.opExtrude","SWEPT_FACE",FACE,{"disambiguationData":[OSD([sQuery(id+"F2.wireOp",EDGE,"E2.4.0.3")])]})]}),makeQuery(id+"F5.opExtrude","SWEPT_FACE",FACE,{"disambiguationData":[OSD([sQuery(id+"F4.wireOp",EDGE,"E5.top")])]}),makeQuery(id+"F5.opExtrude","SWEPT_FACE",FACE,{"disambiguationData":[OSD([sQuery(id+"F4.wireOp",EDGE,"E6.1.0.5")])]}),makeQuery(id+"F5.opExtrude","SWEPT_FACE",FACE,{"disambiguationData":[OSD([sQuery(id+"F4.wireOp",EDGE,"E6.2.0.5")])]}),makeQuery(id+"F5.opExtrude","SWEPT_FACE",FACE,{"disambiguationData":[OSD([sQuery(id+"F4.wireOp",EDGE,"E6.3.0.5")])]})]})]});
            var Q8;
            Q8=makeQuery(id+"F7.opChamfer","BLEND_EDGE",EDGE,{"blendedFrom":[makeQuery(id+"F5.opExtrude","CAP_EDGE",EDGE,{"disambiguationData":[OSD([sQuery(id+"F4.wireOp",EDGE,"E7.3.4.0")])],"isStart":false}),makeQuery(id+"F5.boolean.opBoolean","MERGE",FACE,{"derivedFrom":[makeQuery(id+"F3.boolean.opBoolean","MERGE",FACE,{"derivedFrom":[makeQuery(id+"F1.opExtrude","SWEPT_FACE",FACE,{"disambiguationData":[OSD([sQuery(id+"F0.wireOp",EDGE,"E0.rect.bottom")])]}),makeQuery(id+"F3.opExtrude","SWEPT_FACE",FACE,{"disambiguationData":[OSD([sQuery(id+"F2.wireOp",EDGE,"E1.bottom")])]}),makeQuery(id+"F3.opExtrude","SWEPT_FACE",FACE,{"disambiguationData":[OSD([sQuery(id+"F2.wireOp",EDGE,"E2.1.0.2")])]}),makeQuery(id+"F3.opExtrude","SWEPT_FACE",FACE,{"disambiguationData":[OSD([sQuery(id+"F2.wireOp",EDGE,"E2.2.0.2")])]}),makeQuery(id+"F3.opExtrude","SWEPT_FACE",FACE,{"disambiguationData":[OSD([sQuery(id+"F2.wireOp",EDGE,"E2.3.0.2")])]}),makeQuery(id+"F3.opExtrude","SWEPT_FACE",FACE,{"disambiguationData":[OSD([sQuery(id+"F2.wireOp",EDGE,"E2.4.0.2")])]}),makeQuery(id+"F3.opExtrude","SWEPT_FACE",FACE,{"disambiguationData":[OSD([sQuery(id+"F2.wireOp",EDGE,"E3.6.5.0")])]})]}),makeQuery(id+"F5.opExtrude","SWEPT_FACE",FACE,{"disambiguationData":[OSD([sQuery(id+"F4.wireOp",EDGE,"E4.bottom")])]}),makeQuery(id+"F5.opExtrude","SWEPT_FACE",FACE,{"disambiguationData":[OSD([sQuery(id+"F4.wireOp",EDGE,"E6.1.0.0")])]}),makeQuery(id+"F5.opExtrude","SWEPT_FACE",FACE,{"disambiguationData":[OSD([sQuery(id+"F4.wireOp",EDGE,"E6.2.0.0")])]}),makeQuery(id+"F5.opExtrude","SWEPT_FACE",FACE,{"disambiguationData":[OSD([sQuery(id+"F4.wireOp",EDGE,"E6.3.0.0")])]}),makeQuery(id+"F5.opExtrude","SWEPT_FACE",FACE,{"disambiguationData":[OSD([sQuery(id+"F4.wireOp",EDGE,"E7.0.4.0")])]})]})],"blendedInto":[makeQuery(id+"F5.boolean.opBoolean","MERGE",FACE,{"derivedFrom":[makeQuery(id+"F3.boolean.opBoolean","MERGE",FACE,{"derivedFrom":[makeQuery(id+"F1.opExtrude","SWEPT_FACE",FACE,{"disambiguationData":[OSD([sQuery(id+"F0.wireOp",EDGE,"E0.rect.bottom")])]}),makeQuery(id+"F3.opExtrude","SWEPT_FACE",FACE,{"disambiguationData":[OSD([sQuery(id+"F2.wireOp",EDGE,"E1.bottom")])]}),makeQuery(id+"F3.opExtrude","SWEPT_FACE",FACE,{"disambiguationData":[OSD([sQuery(id+"F2.wireOp",EDGE,"E2.1.0.2")])]}),makeQuery(id+"F3.opExtrude","SWEPT_FACE",FACE,{"disambiguationData":[OSD([sQuery(id+"F2.wireOp",EDGE,"E2.2.0.2")])]}),makeQuery(id+"F3.opExtrude","SWEPT_FACE",FACE,{"disambiguationData":[OSD([sQuery(id+"F2.wireOp",EDGE,"E2.3.0.2")])]}),makeQuery(id+"F3.opExtrude","SWEPT_FACE",FACE,{"disambiguationData":[OSD([sQuery(id+"F2.wireOp",EDGE,"E2.4.0.2")])]}),makeQuery(id+"F3.opExtrude","SWEPT_FACE",FACE,{"disambiguationData":[OSD([sQuery(id+"F2.wireOp",EDGE,"E3.6.5.0")])]})]}),makeQuery(id+"F5.opExtrude","SWEPT_FACE",FACE,{"disambiguationData":[OSD([sQuery(id+"F4.wireOp",EDGE,"E4.bottom")])]}),makeQuery(id+"F5.opExtrude","SWEPT_FACE",FACE,{"disambiguationData":[OSD([sQuery(id+"F4.wireOp",EDGE,"E6.1.0.0")])]}),makeQuery(id+"F5.opExtrude","SWEPT_FACE",FACE,{"disambiguationData":[OSD([sQuery(id+"F4.wireOp",EDGE,"E6.2.0.0")])]}),makeQuery(id+"F5.opExtrude","SWEPT_FACE",FACE,{"disambiguationData":[OSD([sQuery(id+"F4.wireOp",EDGE,"E6.3.0.0")])]}),makeQuery(id+"F5.opExtrude","SWEPT_FACE",FACE,{"disambiguationData":[OSD([sQuery(id+"F4.wireOp",EDGE,"E7.0.4.0")])]})]})]});
            var Q9;
            Q9=makeQuery(id+"F7.opChamfer","BLEND_EDGE",EDGE,{"blendedFrom":[makeQuery(id+"F5.opExtrude","CAP_EDGE",EDGE,{"disambiguationData":[OSD([sQuery(id+"F4.wireOp",EDGE,"E7.12.4.0")])],"isStart":false}),makeQuery(id+"F5.boolean.opBoolean","MERGE",FACE,{"derivedFrom":[makeQuery(id+"F3.boolean.opBoolean","MERGE",FACE,{"derivedFrom":[makeQuery(id+"F1.opExtrude","SWEPT_FACE",FACE,{"disambiguationData":[OSD([sQuery(id+"F0.wireOp",EDGE,"E0.rect.top")])]}),makeQuery(id+"F3.opExtrude","SWEPT_FACE",FACE,{"disambiguationData":[OSD([sQuery(id+"F2.wireOp",EDGE,"E1.top")])]}),makeQuery(id+"F3.opExtrude","SWEPT_FACE",FACE,{"disambiguationData":[OSD([sQuery(id+"F2.wireOp",EDGE,"E2.1.0.3")])]}),makeQuery(id+"F3.opExtrude","SWEPT_FACE",FACE,{"disambiguationData":[OSD([sQuery(id+"F2.wireOp",EDGE,"E2.2.0.3")])]}),makeQuery(id+"F3.opExtrude","SWEPT_FACE",FACE,{"disambiguationData":[OSD([sQuery(id+"F2.wireOp",EDGE,"E2.3.0.3")])]}),makeQuery(id+"F3.opExtrude","SWEPT_FACE",FACE,{"disambiguationData":[OSD([sQuery(id+"F2.wireOp",EDGE,"E2.4.0.3")])]}),makeQuery(id+"F3.opExtrude","SWEPT_FACE",FACE,{"disambiguationData":[OSD([sQuery(id+"F2.wireOp",EDGE,"E3.9.5.0")])]})]}),makeQuery(id+"F5.opExtrude","SWEPT_FACE",FACE,{"disambiguationData":[OSD([sQuery(id+"F4.wireOp",EDGE,"E5.top")])]}),makeQuery(id+"F5.opExtrude","SWEPT_FACE",FACE,{"disambiguationData":[OSD([sQuery(id+"F4.wireOp",EDGE,"E6.1.0.5")])]}),makeQuery(id+"F5.opExtrude","SWEPT_FACE",FACE,{"disambiguationData":[OSD([sQuery(id+"F4.wireOp",EDGE,"E6.2.0.5")])]}),makeQuery(id+"F5.opExtrude","SWEPT_FACE",FACE,{"disambiguationData":[OSD([sQuery(id+"F4.wireOp",EDGE,"E6.3.0.5")])]}),makeQuery(id+"F5.opExtrude","SWEPT_FACE",FACE,{"disambiguationData":[OSD([sQuery(id+"F4.wireOp",EDGE,"E7.15.4.0")])]})]})],"blendedInto":[makeQuery(id+"F5.boolean.opBoolean","MERGE",FACE,{"derivedFrom":[makeQuery(id+"F3.boolean.opBoolean","MERGE",FACE,{"derivedFrom":[makeQuery(id+"F1.opExtrude","SWEPT_FACE",FACE,{"disambiguationData":[OSD([sQuery(id+"F0.wireOp",EDGE,"E0.rect.top")])]}),makeQuery(id+"F3.opExtrude","SWEPT_FACE",FACE,{"disambiguationData":[OSD([sQuery(id+"F2.wireOp",EDGE,"E1.top")])]}),makeQuery(id+"F3.opExtrude","SWEPT_FACE",FACE,{"disambiguationData":[OSD([sQuery(id+"F2.wireOp",EDGE,"E2.1.0.3")])]}),makeQuery(id+"F3.opExtrude","SWEPT_FACE",FACE,{"disambiguationData":[OSD([sQuery(id+"F2.wireOp",EDGE,"E2.2.0.3")])]}),makeQuery(id+"F3.opExtrude","SWEPT_FACE",FACE,{"disambiguationData":[OSD([sQuery(id+"F2.wireOp",EDGE,"E2.3.0.3")])]}),makeQuery(id+"F3.opExtrude","SWEPT_FACE",FACE,{"disambiguationData":[OSD([sQuery(id+"F2.wireOp",EDGE,"E2.4.0.3")])]}),makeQuery(id+"F3.opExtrude","SWEPT_FACE",FACE,{"disambiguationData":[OSD([sQuery(id+"F2.wireOp",EDGE,"E3.9.5.0")])]})]}),makeQuery(id+"F5.opExtrude","SWEPT_FACE",FACE,{"disambiguationData":[OSD([sQuery(id+"F4.wireOp",EDGE,"E5.top")])]}),makeQuery(id+"F5.opExtrude","SWEPT_FACE",FACE,{"disambiguationData":[OSD([sQuery(id+"F4.wireOp",EDGE,"E6.1.0.5")])]}),makeQuery(id+"F5.opExtrude","SWEPT_FACE",FACE,{"disambiguationData":[OSD([sQuery(id+"F4.wireOp",EDGE,"E6.2.0.5")])]}),makeQuery(id+"F5.opExtrude","SWEPT_FACE",FACE,{"disambiguationData":[OSD([sQuery(id+"F4.wireOp",EDGE,"E6.3.0.5")])]}),makeQuery(id+"F5.opExtrude","SWEPT_FACE",FACE,{"disambiguationData":[OSD([sQuery(id+"F4.wireOp",EDGE,"E7.15.4.0")])]})]})]});
            fillet(context, id + "F8", {"entities" : qUnion([Q0, Q1, Q2, Q3, Q4, Q5, Q6, Q7, Q8, Q9]), "radius" : 2 * mm, "tangentPropagation" : true, "allowEdgeOverflow" : false});
        }
        {
            var Q0;
            Q0=makeQuery(id+"F3.boolean.opBoolean","MERGE",FACE,{"derivedFrom":[makeQuery(id+"F1.opExtrude","SWEPT_FACE",FACE,{"disambiguationData":[OSD([sQuery(id+"F0.wireOp",EDGE,"E0.rect.left")])]}),makeQuery(id+"F3.opExtrude","SWEPT_FACE",FACE,{"disambiguationData":[OSD([sQuery(id+"F2.wireOp",EDGE,"E1.left")])]})]});
            var sketch = newSketch(context, id + "F9", { "sketchPlane" : qUnion([Q0])});
            skText(sketch, "E8", { "text": "MKTR\n", "fontName": "OpenSans-Bold.ttf"});
            const initialGuessF9  = {"E8": [-0.04, 0.004, 1, 0, 0.02024]};
            skSetInitialGuess(sketch, initialGuessF9);
            skSolve(sketch);
        }
        {
            var Q0;
            Q0 = qSketchRegion(id + "F9", true);
            extrude(context, id + "F10", {"entities" : qUnion([Q0]), "operationType" : NewBodyOperationType.REMOVE, "oppositeDirection" : true, "depth" : 0.5 * mm});
        }
    });
